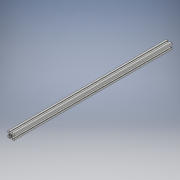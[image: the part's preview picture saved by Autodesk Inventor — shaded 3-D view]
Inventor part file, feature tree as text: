
AUTODESK INVENTOR PART (.ipt)
format: ipt  version: 2025 (Build 290162000, 162)  size: 240,640 bytes
history: native  units: mm
features: extrude x1, sketch x1
ambient origin geometry x8: Origin, YZ Plane, XZ Plane, XY Plane, X Axis, Y Axis, Z Axis, Center Point
bodies: Solid1 (feature_tree)
feature tree (2):
  extrude  "Extrusion1"  [1 undecoded]
  sketch  "Sketch_1"  dims[d0=500.0mm d1=0.0mm]
note: 1 required parameter value undecoded (feature->parameter linkage not recoverable at this tier; creation-order binding heuristic only, values carry confidence <= 0.55)
